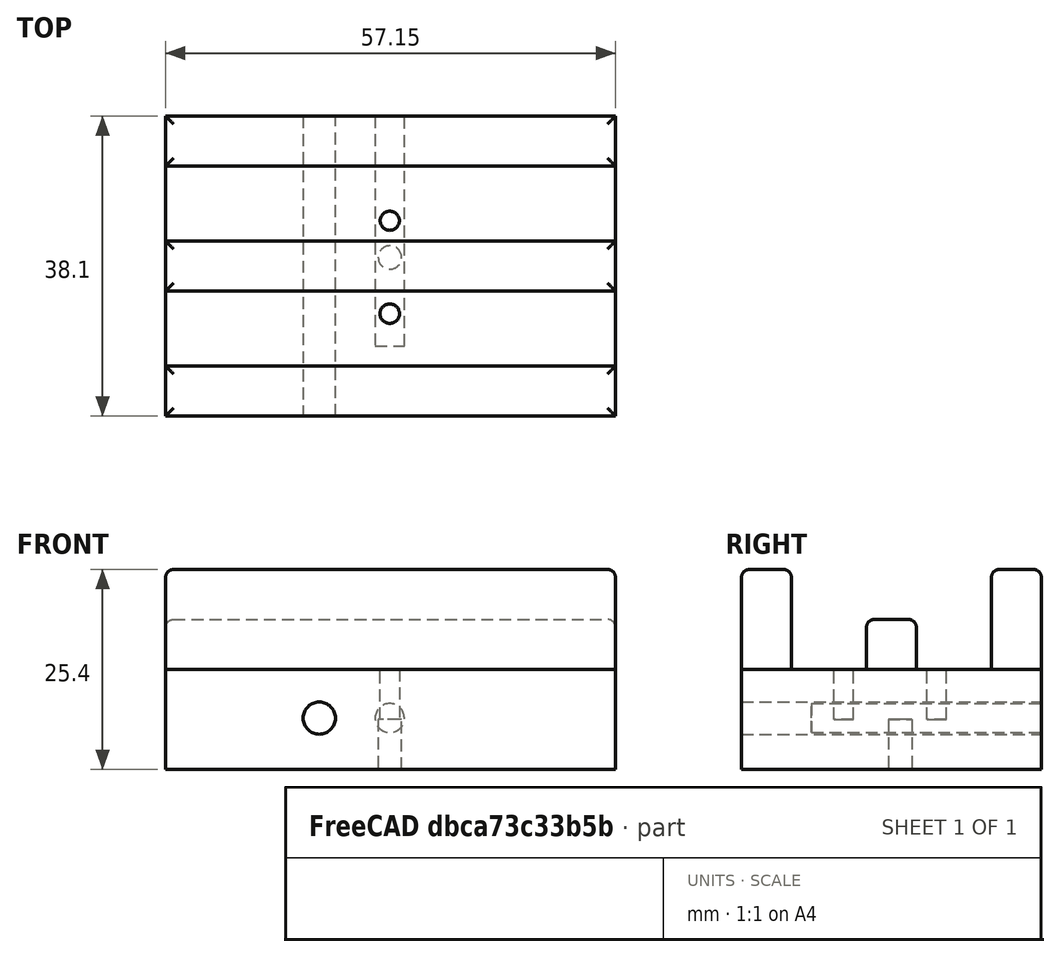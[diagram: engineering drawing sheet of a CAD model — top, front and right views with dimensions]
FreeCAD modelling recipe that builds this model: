
FCSTD DOCUMENT  (FreeCAD 0.15R4671 (Git))
Label: greaseninja
License: All rights reserved
LicenseURL: http://en.wikipedia.org/wiki/All_rights_reserved
objects: Part::Box×4, Sketcher::SketchObject×4, PartDesign::Pocket×4, Part::Fillet×3
note: 19 computed .brp shape members not serialized (recipe doc carries the construction recipe); baked Part::Feature solids carry a one-line shape summary decoded from their .brp

FEATURE [Part::Box] Box  label="Cube"
  Height = 12.7
  Length = 57.15
  Width = 38.1
FEATURE [Part::Box] Box001  label="Cube001"
  Height = 12.7
  Length = 57.15
  Placement = pos=(0,0,12.7) rot=(0,0,1;0rad)
  Width = 6.35
FEATURE [Part::Box] Box002  label="Cube002"
  Height = 12.7
  Length = 57.15
  Placement = pos=(0,31.75,12.7) rot=(0,0,1;0rad)
  Width = 6.35
FEATURE [Part::Box] Box003  label="Cube003"
  Height = 6.35
  Length = 57.15
  Placement = pos=(0,15.875,12.7) rot=(0,0,1;0rad)
  Width = 6.35
FEATURE [Sketcher::SketchObject] Sketch
  Placement = pos=(0,0,12.7) rot=(0,0,1;0rad)
  Support = -> Box [Face6]
  sketch-geometry (2):
    g0: Circle CenterX=28.4759 CenterY=12.9939 CenterZ=0 NormalX=0 NormalY=0 NormalZ=1 Radius=1.23961
    g1: Circle CenterX=28.4759 CenterY=24.8049 CenterZ=0 NormalX=0 NormalY=0 NormalZ=1 Radius=1.21972
FEATURE [PartDesign::Pocket] Pocket
  Length = 6.35
  Sketch = -> Sketch
  Type = 0
FEATURE [Sketcher::SketchObject] Sketch001
  Placement = pos=(0,38.1,0) rot=(0,0.707107,0.707107;3.14159rad)
  Support = -> Pocket [Face4]
  sketch-geometry (1):
    g0: Circle CenterX=-28.4775 CenterY=6.52411 CenterZ=0 NormalX=0 NormalY=0 NormalZ=1 Radius=1.84928
FEATURE [PartDesign::Pocket] Pocket001
  Length = 29.21
  Sketch = -> Sketch001
  Type = 0
FEATURE [Sketcher::SketchObject] Sketch002
  Placement = pos=(0,38.1,0) rot=(0,0.707107,0.707107;3.14159rad)
  Support = -> Pocket001 [Face4]
  sketch-geometry (1):
    g0: Circle CenterX=-19.5247 CenterY=6.52411 CenterZ=0 NormalX=0 NormalY=0 NormalZ=1 Radius=2.04494
FEATURE [PartDesign::Pocket] Pocket002
  Length = 38.1
  Sketch = -> Sketch002
  Type = 0
FEATURE [Sketcher::SketchObject] Sketch003
  Placement = pos=(0,0,0) rot=(1,0,0;3.14159rad)
  Support = -> Pocket002 [Face5]
  sketch-geometry (1):
    g0: Circle CenterX=28.5006 CenterY=-20.1356 CenterZ=0 NormalX=0 NormalY=0 NormalZ=1 Radius=1.48977
FEATURE [PartDesign::Pocket] Pocket003
  Length = 6.35
  Sketch = -> Sketch003
  Type = 0
FEATURE [Part::Fillet] Fillet
  Base = -> Box001
  Edges = 4 edges r=1: [Edge2,Edge6,Edge10,Edge12]
FEATURE [Part::Fillet] Fillet001
  Base = -> Box002
  Edges = 4 edges r=1: [Edge2,Edge6,Edge10,Edge12]
FEATURE [Part::Fillet] Fillet002
  Base = -> Box003
  Edges = 4 edges r=1: [Edge2,Edge6,Edge10,Edge12]
